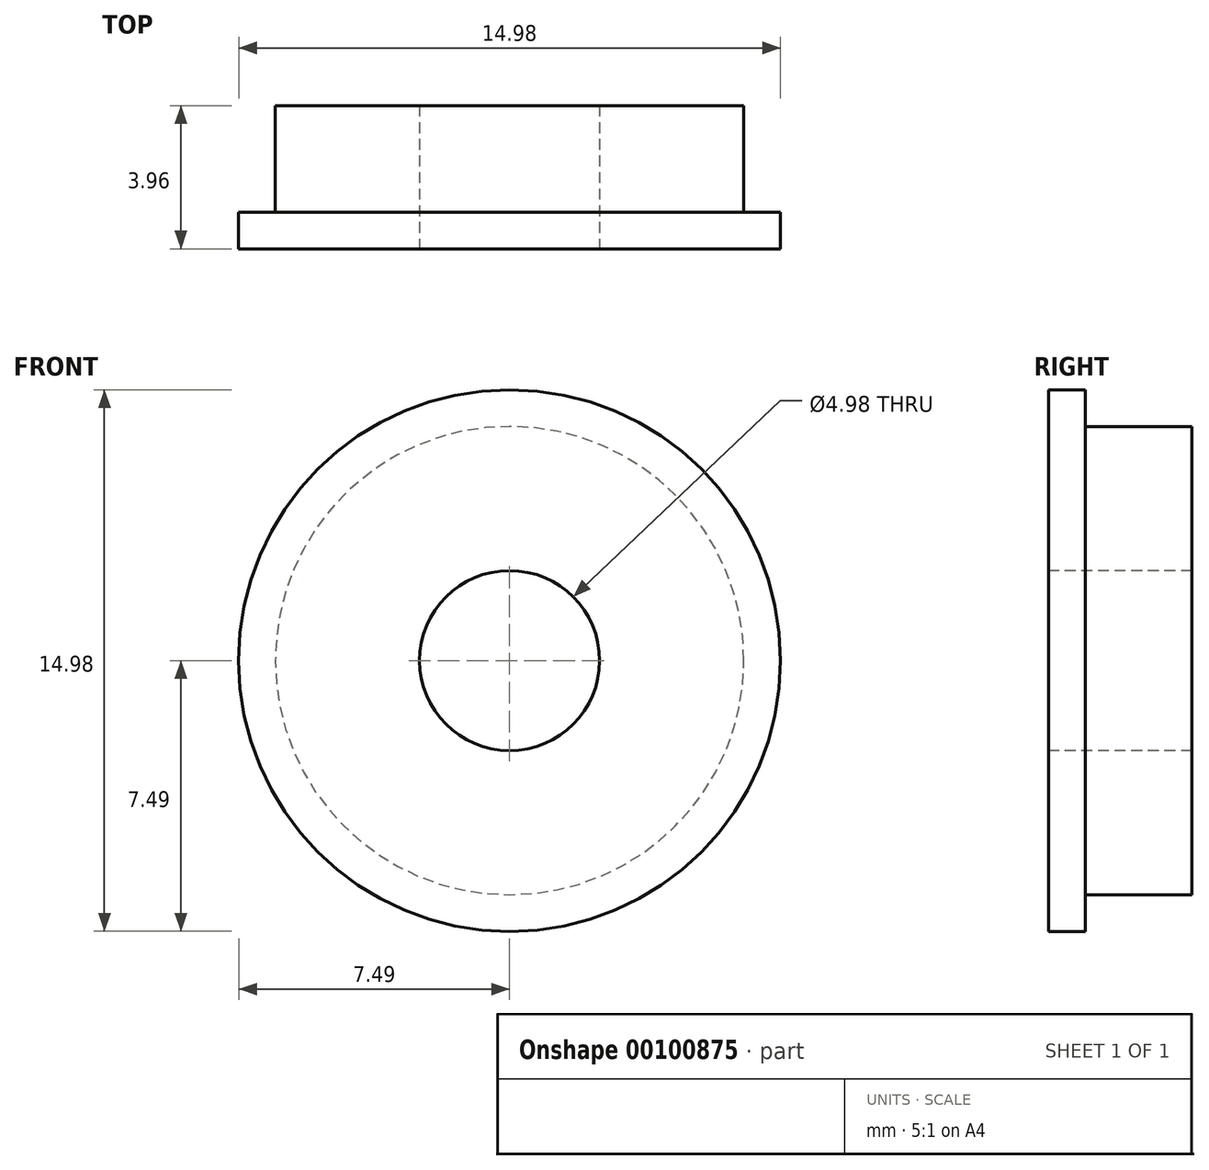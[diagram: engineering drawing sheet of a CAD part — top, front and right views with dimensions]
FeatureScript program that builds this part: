
annotation { "Feature Type Name" : "Feature", "Feature Type Description" : "" }
export const myFeature = defineFeature(function(context is Context, id is Id, definition is map)
    precondition{}
    {
        {
            var Q0;
            Q0=qCreatedBy(makeId("Right.planeOp"),FACE);
            var sketch = newSketch(context, id + "F0", { "sketchPlane" : qUnion([Q0])});
            skLineSegment(sketch, "E0", {"start": v(0, 2.49) * mm, "end": v(0, 7.5) * mm});
            skLineSegment(sketch, "E1", {"start": v(0, 7.5) * mm, "end": v(1.02, 7.5) * mm});
            skLineSegment(sketch, "E2", {"start": v(1.02, 7.5) * mm, "end": v(1.02, 6.48) * mm});
            skLineSegment(sketch, "E3", {"start": v(1.02, 6.48) * mm, "end": v(3.96, 6.48) * mm});
            skLineSegment(sketch, "E4", {"start": v(3.96, 6.48) * mm, "end": v(3.96, 2.49) * mm});
            skLineSegment(sketch, "E5", {"start": v(3.96, 2.49) * mm, "end": v(0, 2.49) * mm});
            skLineSegment(sketch, "E6", {"start": v(0, 0) * mm, "end": v(11.24, 0) * mm, "construction": true});
            skSolve(sketch);
        }
        {
            var Q0;
            Q0 = qSketchRegion(id + "F0", true);
            var Q1;
            Q1=sQuery(id+"F0.wireOp",EDGE,"E6");
            revolve(context, id + "F1", {"entities" : qUnion([Q0]), "axis" : qUnion([Q1]), "revolveType" : RevolveType.FULL});
        }
    });
